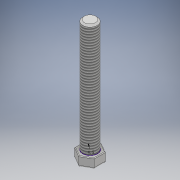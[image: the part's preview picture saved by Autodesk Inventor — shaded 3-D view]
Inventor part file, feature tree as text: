
AUTODESK INVENTOR PART (.ipt)
format: ipt  version: 2018 (Build 220112000, 112)  size: 145,408 bytes
history: native  units: mm
features: sketch x4, extrude x3, fillet x2, thread x1, chamfer x1
ambient origin geometry x8: Origin, YZ Plane, XZ Plane, XY Plane, X Axis, Y Axis, Z Axis, Center Point
bodies: 实体1 (feature_tree)
feature tree (11):
  sketch  "草图1"  dims[d0=4.5mm d1=35.0mm d2=0.0mm d3=10.0mm d4=0.0mm]
  extrude  "拉伸1"  Depth=35.0mm TaperAngle=0.0deg
  thread  "螺纹1"  [1 undecoded]
  sketch  "草图4"  dims[d16=3.0mm d17=0.0mm d18=0.5mm d19=0.2mm d20=3.0mm]
  sketch  "草图5"  dims[d21=2.0mm d22=0.0mm d23=0.5mm d24=2.0mm d25=45.0deg]
  extrude  "拉伸4"  Depth=0.5mm
  fillet  "圆角3"  Radius=0.2mm
  fillet  "圆角4"  Radius=3.0mm
  extrude  "拉伸5"  Depth=0.5mm TaperAngle=45.0deg
  chamfer  "倒角1"  [1 undecoded]
  sketch  "草图6"
note: 2 required parameter values undecoded (feature->parameter linkage not recoverable at this tier; creation-order binding heuristic only, values carry confidence <= 0.55)
